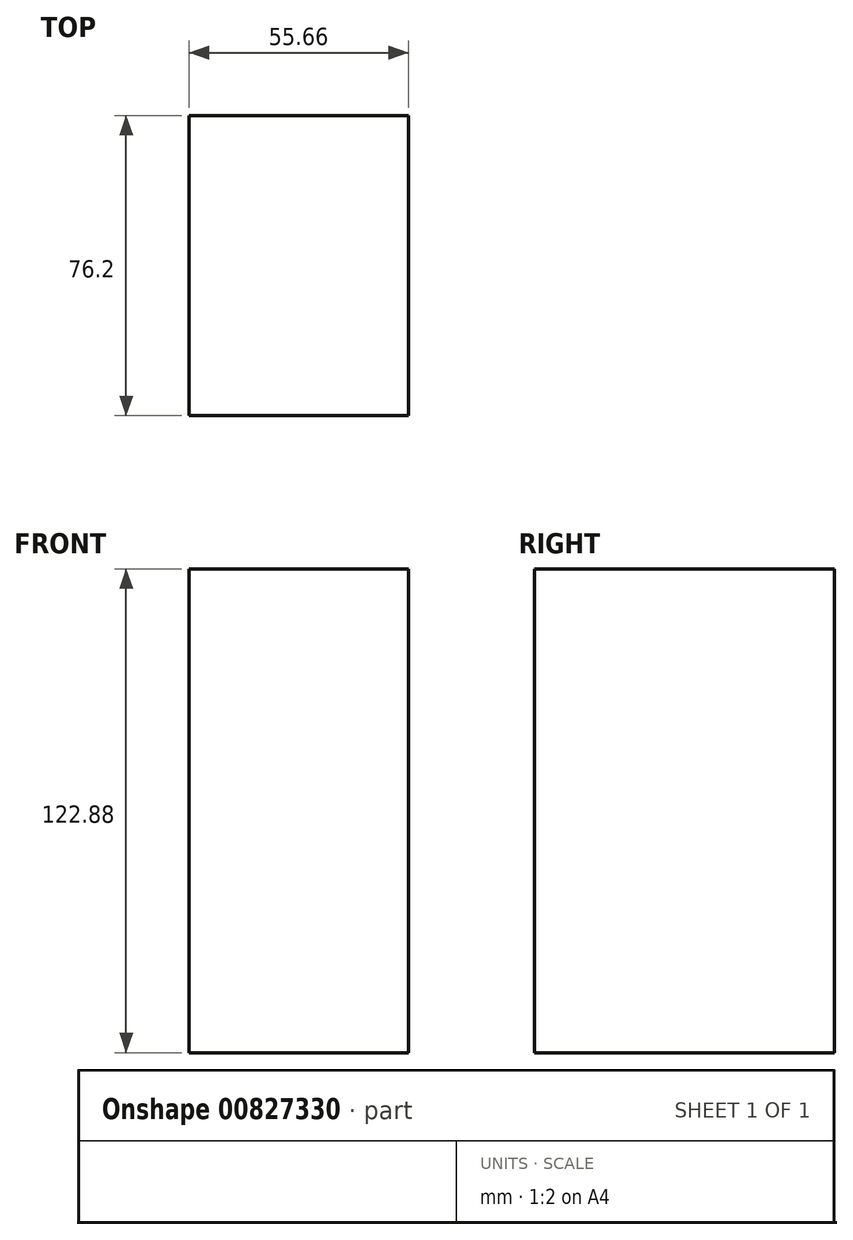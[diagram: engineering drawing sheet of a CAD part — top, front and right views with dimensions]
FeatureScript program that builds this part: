
annotation { "Feature Type Name" : "Feature", "Feature Type Description" : "" }
export const myFeature = defineFeature(function(context is Context, id is Id, definition is map)
    precondition{}
    {
        {
            var Q0;
            Q0=qCreatedBy(makeId("Front.planeOp"),FACE);
            var sketch = newSketch(context, id + "F0", { "sketchPlane" : qUnion([Q0])});
            skLineSegment(sketch, "E0.bottom", {"start": v(27.83, 61.44) * mm, "end": v(-27.83, 61.44) * mm});
            skLineSegment(sketch, "E0.top", {"start": v(27.83, -61.44) * mm, "end": v(-27.83, -61.44) * mm});
            skLineSegment(sketch, "E0.left", {"start": v(27.83, 61.44) * mm, "end": v(27.83, -61.44) * mm});
            skLineSegment(sketch, "E0.right", {"start": v(-27.83, 61.44) * mm, "end": v(-27.83, -61.44) * mm});
            skPoint(sketch, "E0.middle", {"position": v(0, 0) * mm});
            skSolve(sketch);
        }
        {
            var Q0;
            Q0 = qSketchRegion(id + "F0", true);
            extrude(context, id + "F1", {"entities" : qUnion([Q0]), "depth" : 76.2 * mm, "offsetDistance" : 25.4 * mm});
        }
    });
